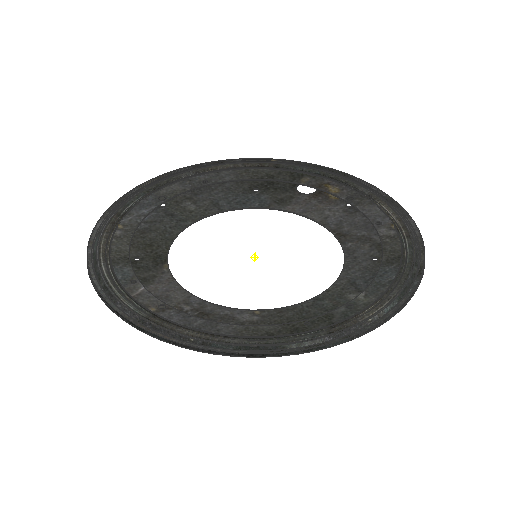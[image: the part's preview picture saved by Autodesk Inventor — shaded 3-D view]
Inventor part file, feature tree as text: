
AUTODESK INVENTOR PART (.ipt)
format: ipt  version: 2025.1 (Build 291241020, 241B)  size: 782,336 bytes
history: native  units: in
note: dims shown in document units (in); Inventor stores cm internally (conversion verified against a paired STEP export)
features: other x17, revolve x1
ambient origin geometry x8: Origin, YZ Plane, XZ Plane, XY Plane, X Axis, Y Axis, Z Axis, Center Point
bodies: Solid1 (feature_tree), Solid2 (feature_tree), Solid3 (feature_tree), Solid4 (feature_tree), Solid5 (feature_tree), Solid6 (feature_tree), Solid7 (feature_tree), Solid8 (feature_tree), Solid9 (feature_tree), Solid10 (feature_tree), Solid11 (feature_tree), Solid12 (feature_tree), Solid13 (feature_tree), Solid14 (feature_tree), Solid15 (feature_tree), Solid16 (feature_tree), Solid17 (feature_tree), Solid18 (feature_tree)
feature tree (18):
  revolve  "Revolve1"  [1 undecoded]
  other  "CirPattern5[1]"
  other  "CirPattern5[2]"
  other  "CirPattern5[3]"
  other  "CirPattern5[4]"
  other  "CirPattern5[5]"
  other  "CirPattern5[6]"
  other  "CirPattern5[7]"
  other  "CirPattern5[8]"
  other  "Cut-Extrude5[1]"
  other  "Cut-Extrude5[2]"
  other  "Cut-Extrude5[3]"
  other  "Cut-Extrude5[4]"
  other  "Cut-Extrude5[5]"
  other  "Cut-Extrude6"
  other  "CirPattern5[9]"
  other  "CirPattern5[10]"
  other  "CirPattern5[11]"
note: 1 required parameter value undecoded (feature->parameter linkage not recoverable at this tier; creation-order binding heuristic only, values carry confidence <= 0.55)
